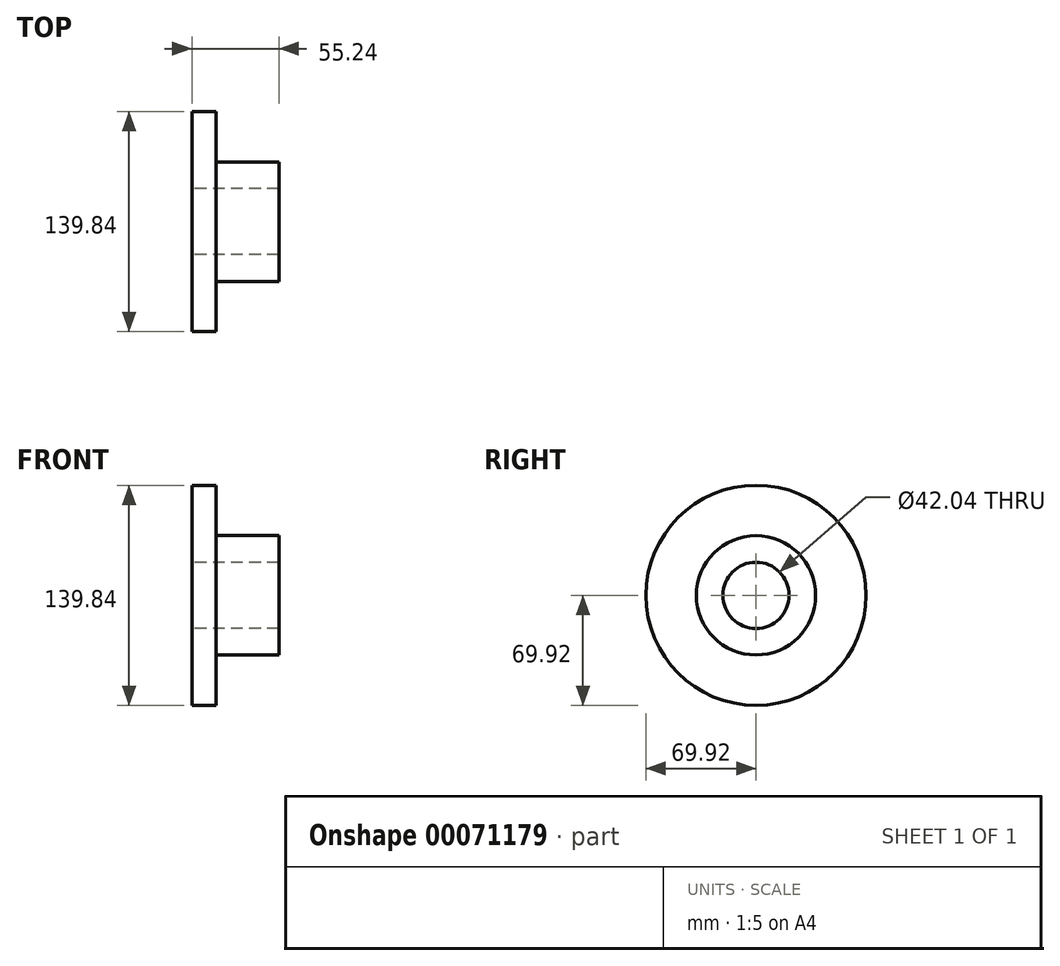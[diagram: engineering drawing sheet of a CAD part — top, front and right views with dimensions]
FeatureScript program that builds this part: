
annotation { "Feature Type Name" : "Feature", "Feature Type Description" : "" }
export const myFeature = defineFeature(function(context is Context, id is Id, definition is map)
    precondition{}
    {
        {
            var Q0;
            Q0=qCreatedBy(makeId("Front.planeOp"),FACE);
            var sketch = newSketch(context, id + "F1", { "sketchPlane" : qUnion([Q0])});
            skLineSegment(sketch, "E0", {"start": v(0, 0) * mm, "end": v(55.24, 0) * mm});
            skLineSegment(sketch, "E1.bottom", {"start": v(0, 21.02) * mm, "end": v(15.15, 21.02) * mm});
            skLineSegment(sketch, "E1.top", {"start": v(0, 69.92) * mm, "end": v(15.15, 69.92) * mm});
            skLineSegment(sketch, "E1.left", {"start": v(0, 21.02) * mm, "end": v(0, 69.92) * mm});
            skLineSegment(sketch, "E1.right", {"start": v(15.15, 21.02) * mm, "end": v(15.15, 69.92) * mm});
            skLineSegment(sketch, "E2.bottom", {"start": v(0, 21.02) * mm, "end": v(55.24, 21.02) * mm});
            skLineSegment(sketch, "E2.top", {"start": v(0, 37.88) * mm, "end": v(55.24, 37.88) * mm});
            skLineSegment(sketch, "E2.left", {"start": v(0, 21.02) * mm, "end": v(0, 37.88) * mm});
            skLineSegment(sketch, "E2.right", {"start": v(55.24, 21.02) * mm, "end": v(55.24, 37.88) * mm});
            skSolve(sketch);
        }
        {
            var Q0;
            Q0 = qSketchRegion(id + "F1", true);
            var Q1;
            Q1=sQuery(id+"F1.wireOp",EDGE,"E0");
            revolve(context, id + "F0", {"entities" : qUnion([Q0]), "axis" : qUnion([Q1]), "revolveType" : RevolveType.FULL});
        }
    });
